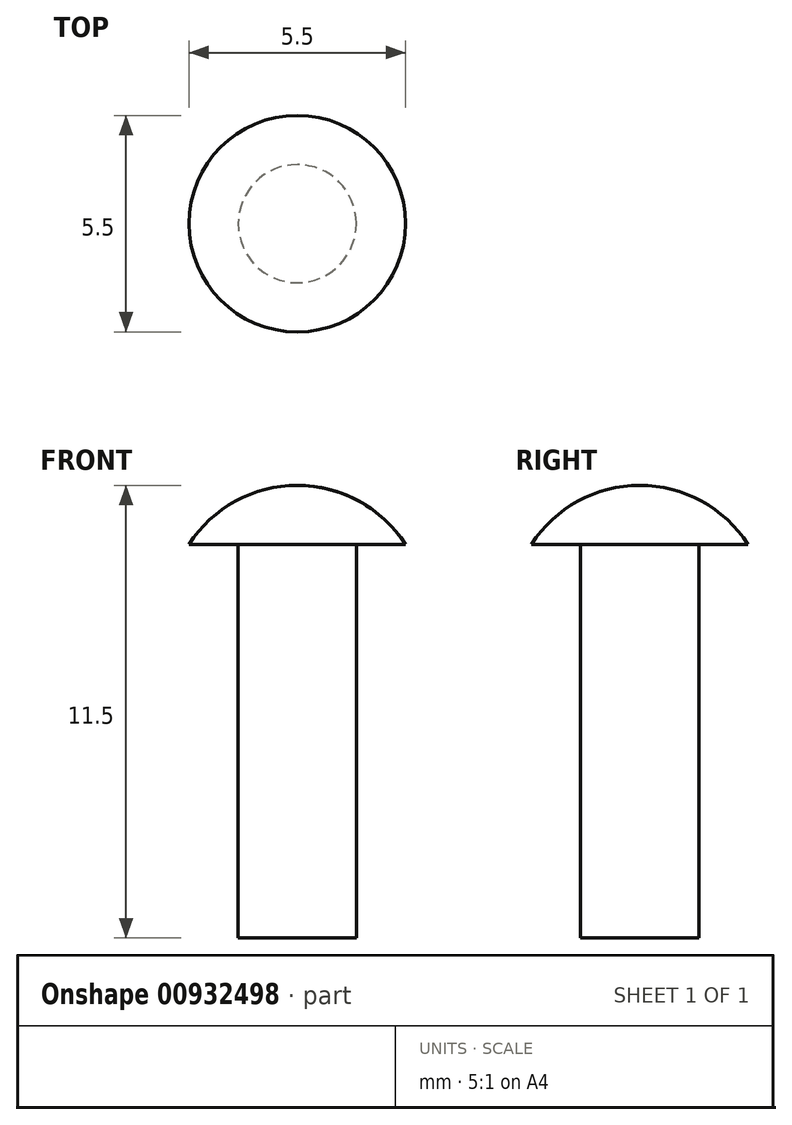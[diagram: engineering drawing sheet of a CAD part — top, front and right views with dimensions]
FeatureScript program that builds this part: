
annotation { "Feature Type Name" : "Feature", "Feature Type Description" : "" }
export const myFeature = defineFeature(function(context is Context, id is Id, definition is map)
    precondition{}
    {
        {
            var Q0;
            Q0=qCreatedBy(makeId("Front.planeOp"),FACE);
            var sketch = newSketch(context, id + "F0", { "sketchPlane" : qUnion([Q0])});
            skLineSegment(sketch, "E0", {"start": v(0, 37.71) * mm, "end": v(0, -35.93) * mm, "construction": true});
            skLineSegment(sketch, "E1", {"start": v(0, 0) * mm, "end": v(1.5, 0) * mm});
            skLineSegment(sketch, "E2", {"start": v(1.5, 0) * mm, "end": v(1.5, 10) * mm});
            skLineSegment(sketch, "E3", {"start": v(1.5, 10) * mm, "end": v(2.75, 10) * mm});
            skArc(sketch, "E4", {"start": v(2.75, 10) * mm, "mid": v(1.57, 11.1) * mm, "end": v(0, 11.5) * mm});
            skLineSegment(sketch, "E5", {"start": v(0, 11.5) * mm, "end": v(0, 0) * mm});
            skSolve(sketch);
        }
        {
            var Q0;
            Q0=makeQuery(id+"F0.imprint","IMPRINT",FACE,{"disambiguationData":[TD([[makeQuery(id+"F0.imprint","IMPRINT",EDGE,{"derivedFrom":sQuery(id+"F0.wireOp",EDGE,"E1")}),1.0]])]});
            var Q1;
            Q1=sQuery(id+"F0.wireOp",EDGE,"E4");
            var Q2;
            Q2=sQuery(id+"F0.wireOp",EDGE,"E3");
            var Q3;
            Q3=sQuery(id+"F0.wireOp",EDGE,"E2");
            var Q4;
            Q4=sQuery(id+"F0.wireOp",EDGE,"E1");
            var Q5;
            Q5=sQuery(id+"F0.wireOp",EDGE,"E0");
            revolve(context, id + "F1", {"surfaceOperationType" : NewSurfaceOperationType.NEW, "entities" : qUnion([Q0]), "surfaceEntities" : qUnion([Q1, Q2, Q3, Q4]), "axis" : qUnion([Q5]), "revolveType" : RevolveType.FULL});
        }
    });
